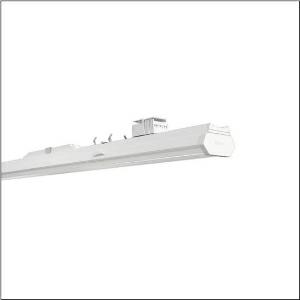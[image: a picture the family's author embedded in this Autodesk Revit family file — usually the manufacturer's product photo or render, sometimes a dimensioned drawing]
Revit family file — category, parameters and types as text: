
# Revit family: licross_r__11_protected_ho_51tp12cn4dxld_10f7
name_source: partatom
category: Lighting Fixtures
units: mm (PartAtom-declared; Revit-internal decimal feet)

## family parameters
Cut with Voids When Loaded = No
Host = Face
Light Source = No
Part Type = Normal
Room Calculation Point = No
Round Connector Dimension = Use Diameter
Shared = No

## types (1)
- --- (1 x LED, 3280 lm, 21.7 W, 4000K)
    Apparent Load = 22 VA
    CIE Flux Codes = 70 91 97 98 100
    Color Rendering = 80
    Color Temperature = 4000K
    Default Elevation = 1800 mm
    Description = Licross® 11 Protected HOluminaire insert, length: 1.500mm, width: 90mm, height: 101mm, LED rated luminous flux: 13.270lm, light colour: 840, control gear: ON/OFF Multilumen, CLOi, control gear: ECG Multilumen, with plug, 6-pole, with phase selection, mains connection: 220..240V, AC/DC, 0/50..60Hz, without changeover relay, for emergency light function, for central battery installations according to DIN EN 60598-2-22, halogen-free wiring, primary optical cover: cover, of PMMA, light emission: direct with ceiling illumination distribution, protection rating (complete): IP64, insulation class (complete): insulation class I (protective earthing), certification: CE, ENEC, VDE, protection symbol: D if used in an environment without relevant dust loads with corresponding accessories, permissible ambient temperature for indoor applications: -35..+40°C, standard: EN 60598-2-22, reducing of maximum allowable ambient temperature of 5°C with ceiling mounting, corresponds to IFS (International Featured Standards) requirements for safety and quality in the food industry, packaging unit: 1 piece
    Height = 92 mm
    Lamp = 1 x LED
    Lamp Light Flux = 3280 lm
    Lamp Power = 21.7 W
    Lamp count = 1
    Length = 1500 mm
    Luminous efficacy = 151 lm/W
    Manufacturer = Siteco
    ModVariant = No
    Model = 51TP12CN4DXLD
    Mounting Place = Ceiling
    Mounting Type = Pendant
    Number of Poles = 1
    OnlyDefault = Yes
    Power Factor = 1
    Product Name = Licross® 11 Protected HO
    Product group = luminaire insert
    ProductGroupID = 902
    Protection Class = Protection class I
    Protection Degree = IP 64
    RLX_Detail_Level = 1
    RlxData = <blob elided: 22149 chars, md5=d837cae2>
    Socket = socket
    Standby Power = 0 W
    System Light Flux = 3280 lm
    System Power = 22 W
    Type Comments = : DC mode (central or group accumulator) initial emergency light level
    Type Image = l_1256148.jpg
    URL = http://relux.com
    VarID = @adj_134767
    Voltage = 0 V
    Weight = 0.00 kg
    Width = 88 mm

## geometry (parser evidence)
native form markers: Blend x4, Sweep x14
no freeform markers — native parametric forms only
